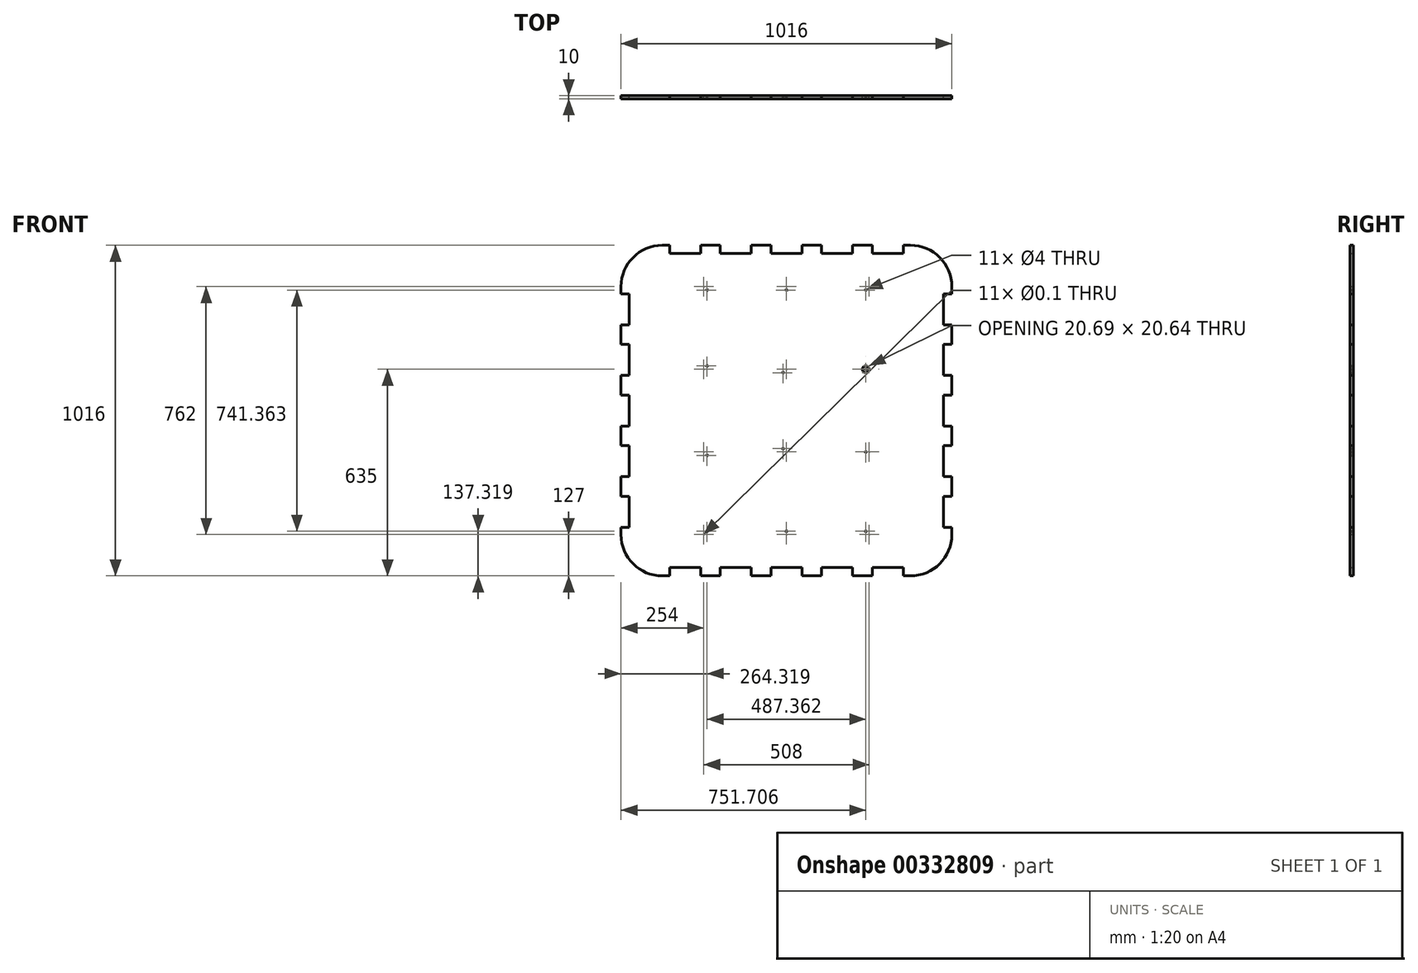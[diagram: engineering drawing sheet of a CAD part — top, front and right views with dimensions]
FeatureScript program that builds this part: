
annotation { "Feature Type Name" : "Feature", "Feature Type Description" : "" }
export const myFeature = defineFeature(function(context is Context, id is Id, definition is map)
    precondition{}
    {
        {
            var Q0;
            Q0=qCreatedBy(makeId("Front.planeOp"),FACE);
            var sketch = newSketch(context, id + "F0", { "sketchPlane" : qUnion([Q0])});
            skLineSegment(sketch, "E0.bottom", {"start": v(508, 508) * mm, "end": v(-508, 508) * mm});
            skLineSegment(sketch, "E0.top", {"start": v(508, -508) * mm, "end": v(-508, -508) * mm});
            skLineSegment(sketch, "E0.left", {"start": v(508, 508) * mm, "end": v(508, -508) * mm});
            skLineSegment(sketch, "E0.right", {"start": v(-508, 508) * mm, "end": v(-508, -508) * mm});
            skPoint(sketch, "E0.middle", {"position": v(0, 0) * mm});
            skCircle(sketch, "E1", {"center": v(-254, 381) * mm, "radius": 0.05 * mm});
            skCircle(sketch, "E2.0.1.0", {"center": v(-254, 127) * mm, "radius": 0.05 * mm});
            skCircle(sketch, "E2.0.2.0", {"center": v(-254, -127) * mm, "radius": 0.05 * mm});
            skCircle(sketch, "E2.1.0.0", {"center": v(0, 381) * mm, "radius": 0.05 * mm});
            skCircle(sketch, "E2.1.1.0", {"center": v(0, 127) * mm, "radius": 0.05 * mm});
            skCircle(sketch, "E2.1.2.0", {"center": v(0, -127) * mm, "radius": 0.05 * mm});
            skCircle(sketch, "E2.2.0.0", {"center": v(254, 381) * mm, "radius": 0.05 * mm});
            skCircle(sketch, "E2.2.1.0", {"center": v(254, 127) * mm, "radius": 0.05 * mm});
            skCircle(sketch, "E2.2.2.0", {"center": v(254, -127) * mm, "radius": 0.05 * mm});
            skLineSegment(sketch, "E2.direction1", {"start": v(-254, 381) * mm, "end": v(0, 381) * mm, "construction": true});
            skLineSegment(sketch, "E2.direction2", {"start": v(-254, 381) * mm, "end": v(-254, 127) * mm, "construction": true});
            skCircle(sketch, "E3.0.0.3", {"center": v(-254, -381) * mm, "radius": 0.05 * mm});
            skCircle(sketch, "E3.0.1.3", {"center": v(0, -381) * mm, "radius": 0.05 * mm});
            skCircle(sketch, "E3.0.2.3", {"center": v(254, -381) * mm, "radius": 0.05 * mm});
            skLineSegment(sketch, "E4", {"start": v(254, 381) * mm, "end": v(0, 381) * mm, "construction": true});
            skLineSegment(sketch, "E5", {"start": v(-254, 381) * mm, "end": v(-254, 126.95) * mm, "construction": true});
            skLineSegment(sketch, "E6", {"start": v(-254, 126.95) * mm, "end": v(0, 127) * mm, "construction": true});
            skLineSegment(sketch, "E7", {"start": v(0, -127) * mm, "end": v(-254, -127) * mm, "construction": true});
            skLineSegment(sketch, "E8", {"start": v(-254, -127) * mm, "end": v(-254, -381) * mm, "construction": true});
            skLineSegment(sketch, "E9", {"start": v(0, 126.95) * mm, "end": v(0, -127) * mm, "construction": true});
            skLineSegment(sketch, "E10", {"start": v(-254, -381) * mm, "end": v(0, -381) * mm, "construction": true});
            skLineSegment(sketch, "E11", {"start": v(0, -381) * mm, "end": v(254, -381) * mm, "construction": true});
            skLineSegment(sketch, "E12", {"start": v(254, -381) * mm, "end": v(254, -127) * mm, "construction": true});
            skLineSegment(sketch, "E13", {"start": v(254, -120.19) * mm, "end": v(254, 127) * mm, "construction": true});
            skLineSegment(sketch, "E14", {"start": v(254, 381) * mm, "end": v(254, 127) * mm, "construction": true});
            skCircle(sketch, "E15", {"center": v(-243.68, 370.68) * mm, "radius": 10.32 * mm});
            skCircle(sketch, "E16", {"center": v(0, 370.68) * mm, "radius": 10.32 * mm});
            skCircle(sketch, "E17", {"center": v(243.68, 370.68) * mm, "radius": 10.32 * mm});
            skCircle(sketch, "E18", {"center": v(-243.68, 370.68) * mm, "radius": 2 * mm});
            skCircle(sketch, "E19", {"center": v(0, 370.68) * mm, "radius": 2 * mm});
            skCircle(sketch, "E20", {"center": v(243.68, 370.68) * mm, "radius": 2 * mm});
            skCircle(sketch, "E21", {"center": v(-243.68, 137.27) * mm, "radius": 10.32 * mm});
            skCircle(sketch, "E22", {"center": v(-243.68, 137.27) * mm, "radius": 2 * mm});
            skCircle(sketch, "E23", {"center": v(-10.32, 116.68) * mm, "radius": 10.32 * mm});
            skCircle(sketch, "E24", {"center": v(-10.32, 116.68) * mm, "radius": 2 * mm});
            skCircle(sketch, "E25.MirrorC", {"center": v(243.68, 127) * mm, "radius": 10.32 * mm});
            skCircle(sketch, "E26.MirrorC", {"center": v(243.68, 127) * mm, "radius": 2 * mm});
            skCircle(sketch, "E27", {"center": v(-10.32, -116.68) * mm, "radius": 10.32 * mm});
            skCircle(sketch, "E28", {"center": v(-10.32, -116.68) * mm, "radius": 2 * mm});
            skCircle(sketch, "E29", {"center": v(-243.68, -137.32) * mm, "radius": 10.32 * mm});
            skCircle(sketch, "E30", {"center": v(-243.68, -137.32) * mm, "radius": 2 * mm});
            skCircle(sketch, "E31", {"center": v(-243.68, -370.68) * mm, "radius": 10.32 * mm});
            skCircle(sketch, "E32", {"center": v(-243.68, -370.68) * mm, "radius": 2 * mm});
            skCircle(sketch, "E33", {"center": v(0, -370.68) * mm, "radius": 2 * mm});
            skCircle(sketch, "E34", {"center": v(0, -370.68) * mm, "radius": 10.32 * mm});
            skCircle(sketch, "E35", {"center": v(243.68, -370.68) * mm, "radius": 10.32 * mm});
            skCircle(sketch, "E36", {"center": v(243.68, -370.68) * mm, "radius": 2 * mm});
            skCircle(sketch, "E37", {"center": v(243.68, -127) * mm, "radius": 2 * mm});
            skCircle(sketch, "E38", {"center": v(243.68, -127) * mm, "radius": 10.32 * mm});
            skLineSegment(sketch, "E39.bottom", {"start": v(-358.77, 508) * mm, "end": v(-263.52, 508) * mm});
            skLineSegment(sketch, "E39.top", {"start": v(-358.77, 482.6) * mm, "end": v(-263.52, 482.6) * mm});
            skLineSegment(sketch, "E39.left", {"start": v(-358.77, 508) * mm, "end": v(-358.77, 482.6) * mm});
            skLineSegment(sketch, "E39.right", {"start": v(-263.52, 508) * mm, "end": v(-263.52, 482.6) * mm});
            skLineSegment(sketch, "E40.bottom", {"start": v(-358.77, -508) * mm, "end": v(-263.52, -508) * mm});
            skLineSegment(sketch, "E40.top", {"start": v(-358.77, -482.6) * mm, "end": v(-263.52, -482.6) * mm});
            skLineSegment(sketch, "E40.left", {"start": v(-358.77, -508) * mm, "end": v(-358.77, -482.6) * mm});
            skLineSegment(sketch, "E40.right", {"start": v(-263.52, -508) * mm, "end": v(-263.52, -482.6) * mm});
            skLineSegment(sketch, "E41.bottom", {"start": v(508, 358.78) * mm, "end": v(482.6, 358.78) * mm});
            skLineSegment(sketch, "E41.top", {"start": v(508, 263.53) * mm, "end": v(482.6, 263.53) * mm});
            skLineSegment(sketch, "E41.left", {"start": v(508, 358.78) * mm, "end": v(508, 263.53) * mm});
            skLineSegment(sketch, "E41.right", {"start": v(482.6, 358.78) * mm, "end": v(482.6, 263.53) * mm});
            skLineSegment(sketch, "E42.bottom", {"start": v(-508, -358.78) * mm, "end": v(-482.6, -358.78) * mm});
            skLineSegment(sketch, "E42.top", {"start": v(-508, -263.53) * mm, "end": v(-482.6, -263.53) * mm});
            skLineSegment(sketch, "E42.left", {"start": v(-508, -358.78) * mm, "end": v(-508, -263.53) * mm});
            skLineSegment(sketch, "E42.right", {"start": v(-482.6, -358.78) * mm, "end": v(-482.6, -263.53) * mm});
            skLineSegment(sketch, "E43.1.0.0", {"start": v(-107.95, 508) * mm, "end": v(-107.95, 482.6) * mm});
            skLineSegment(sketch, "E43.1.0.1", {"start": v(-203.2, 508) * mm, "end": v(-203.2, 482.6) * mm});
            skLineSegment(sketch, "E43.1.0.2", {"start": v(-203.2, 482.6) * mm, "end": v(-107.95, 482.6) * mm});
            skLineSegment(sketch, "E43.2.0.0", {"start": v(47.63, 508) * mm, "end": v(47.63, 482.6) * mm});
            skLineSegment(sketch, "E43.2.0.1", {"start": v(-47.62, 508) * mm, "end": v(-47.62, 482.6) * mm});
            skLineSegment(sketch, "E43.2.0.2", {"start": v(-47.62, 482.6) * mm, "end": v(47.63, 482.6) * mm});
            skLineSegment(sketch, "E43.3.0.0", {"start": v(203.2, 508) * mm, "end": v(203.2, 482.6) * mm});
            skLineSegment(sketch, "E43.3.0.1", {"start": v(107.95, 508) * mm, "end": v(107.95, 482.6) * mm});
            skLineSegment(sketch, "E43.3.0.2", {"start": v(107.95, 482.6) * mm, "end": v(203.2, 482.6) * mm});
            skLineSegment(sketch, "E43.4.0.0", {"start": v(358.78, 508) * mm, "end": v(358.78, 482.6) * mm});
            skLineSegment(sketch, "E43.4.0.1", {"start": v(263.53, 508) * mm, "end": v(263.53, 482.6) * mm});
            skLineSegment(sketch, "E43.4.0.2", {"start": v(263.53, 482.6) * mm, "end": v(358.78, 482.6) * mm});
            skLineSegment(sketch, "E43.direction1", {"start": v(-263.52, 482.6) * mm, "end": v(-107.95, 482.6) * mm, "construction": true});
            skLineSegment(sketch, "E44", {"start": v(-358.77, 495.3) * mm, "end": v(-508, 495.3) * mm, "construction": true});
            skLineSegment(sketch, "E45.0.1.0", {"start": v(508, 203.2) * mm, "end": v(482.6, 203.2) * mm});
            skLineSegment(sketch, "E45.0.1.1", {"start": v(482.6, 203.2) * mm, "end": v(482.6, 107.95) * mm});
            skLineSegment(sketch, "E45.0.1.2", {"start": v(508, 107.95) * mm, "end": v(482.6, 107.95) * mm});
            skLineSegment(sketch, "E45.0.2.0", {"start": v(508, 47.63) * mm, "end": v(482.6, 47.63) * mm});
            skLineSegment(sketch, "E45.0.2.1", {"start": v(482.6, 47.63) * mm, "end": v(482.6, -47.62) * mm});
            skLineSegment(sketch, "E45.0.2.2", {"start": v(508, -47.62) * mm, "end": v(482.6, -47.62) * mm});
            skLineSegment(sketch, "E45.0.3.0", {"start": v(508, -107.95) * mm, "end": v(482.6, -107.95) * mm});
            skLineSegment(sketch, "E45.0.3.1", {"start": v(482.6, -107.95) * mm, "end": v(482.6, -203.2) * mm});
            skLineSegment(sketch, "E45.0.3.2", {"start": v(508, -203.2) * mm, "end": v(482.6, -203.2) * mm});
            skLineSegment(sketch, "E45.0.4.0", {"start": v(508, -263.53) * mm, "end": v(482.6, -263.53) * mm});
            skLineSegment(sketch, "E45.0.4.1", {"start": v(482.6, -263.53) * mm, "end": v(482.6, -358.78) * mm});
            skLineSegment(sketch, "E45.0.4.2", {"start": v(508, -358.78) * mm, "end": v(482.6, -358.78) * mm});
            skLineSegment(sketch, "E45.direction1", {"start": v(482.6, 358.78) * mm, "end": v(494.9, 358.78) * mm, "construction": true});
            skLineSegment(sketch, "E45.direction2", {"start": v(482.6, 358.78) * mm, "end": v(482.6, 203.2) * mm, "construction": true});
            skLineSegment(sketch, "E46.0.1.0", {"start": v(-508, -107.95) * mm, "end": v(-482.6, -107.95) * mm});
            skLineSegment(sketch, "E46.0.1.1", {"start": v(-482.6, -203.2) * mm, "end": v(-482.6, -107.95) * mm});
            skLineSegment(sketch, "E46.0.1.2", {"start": v(-508, -203.2) * mm, "end": v(-482.6, -203.2) * mm});
            skLineSegment(sketch, "E46.0.2.0", {"start": v(-508, 47.62) * mm, "end": v(-482.6, 47.62) * mm});
            skLineSegment(sketch, "E46.0.2.1", {"start": v(-482.6, -47.63) * mm, "end": v(-482.6, 47.62) * mm});
            skLineSegment(sketch, "E46.0.2.2", {"start": v(-508, -47.63) * mm, "end": v(-482.6, -47.63) * mm});
            skLineSegment(sketch, "E46.0.3.0", {"start": v(-508, 203.2) * mm, "end": v(-482.6, 203.2) * mm});
            skLineSegment(sketch, "E46.0.3.1", {"start": v(-482.6, 107.95) * mm, "end": v(-482.6, 203.2) * mm});
            skLineSegment(sketch, "E46.0.3.2", {"start": v(-508, 107.95) * mm, "end": v(-482.6, 107.95) * mm});
            skLineSegment(sketch, "E46.0.4.0", {"start": v(-508, 358.78) * mm, "end": v(-482.6, 358.78) * mm});
            skLineSegment(sketch, "E46.0.4.1", {"start": v(-482.6, 263.53) * mm, "end": v(-482.6, 358.78) * mm});
            skLineSegment(sketch, "E46.0.4.2", {"start": v(-508, 263.53) * mm, "end": v(-482.6, 263.53) * mm});
            skLineSegment(sketch, "E46.direction1", {"start": v(-508, -263.53) * mm, "end": v(-545.7, -263.53) * mm, "construction": true});
            skLineSegment(sketch, "E46.direction2", {"start": v(-508, -263.53) * mm, "end": v(-508, -107.95) * mm, "construction": true});
            skLineSegment(sketch, "E47", {"start": v(494.9, 358.78) * mm, "end": v(494.9, 508) * mm, "construction": true});
            skLineSegment(sketch, "E48", {"start": v(-358.77, -495.3) * mm, "end": v(-508, -495.3) * mm, "construction": true});
            skLineSegment(sketch, "E49.1.0.0", {"start": v(-203.2, -482.6) * mm, "end": v(-107.95, -482.6) * mm});
            skLineSegment(sketch, "E49.1.0.1", {"start": v(-107.95, -508) * mm, "end": v(-107.95, -482.6) * mm});
            skLineSegment(sketch, "E49.1.0.2", {"start": v(-203.2, -508) * mm, "end": v(-203.2, -482.6) * mm});
            skLineSegment(sketch, "E49.2.0.0", {"start": v(-47.62, -482.6) * mm, "end": v(47.63, -482.6) * mm});
            skLineSegment(sketch, "E49.2.0.1", {"start": v(47.63, -508) * mm, "end": v(47.63, -482.6) * mm});
            skLineSegment(sketch, "E49.2.0.2", {"start": v(-47.62, -508) * mm, "end": v(-47.62, -482.6) * mm});
            skLineSegment(sketch, "E49.3.0.0", {"start": v(107.95, -482.6) * mm, "end": v(203.2, -482.6) * mm});
            skLineSegment(sketch, "E49.3.0.1", {"start": v(203.2, -508) * mm, "end": v(203.2, -482.6) * mm});
            skLineSegment(sketch, "E49.3.0.2", {"start": v(107.95, -508) * mm, "end": v(107.95, -482.6) * mm});
            skLineSegment(sketch, "E49.4.0.0", {"start": v(263.53, -482.6) * mm, "end": v(358.78, -482.6) * mm});
            skLineSegment(sketch, "E49.4.0.1", {"start": v(358.78, -508) * mm, "end": v(358.78, -482.6) * mm});
            skLineSegment(sketch, "E49.4.0.2", {"start": v(263.53, -508) * mm, "end": v(263.53, -482.6) * mm});
            skLineSegment(sketch, "E49.direction1", {"start": v(-358.77, -508) * mm, "end": v(-203.2, -508) * mm, "construction": true});
            skLineSegment(sketch, "E50", {"start": v(-495.3, -358.78) * mm, "end": v(-495.3, -508) * mm, "construction": true});
            skSolve(sketch);
        }
        {
            var Q0;
            Q0=makeQuery(id+"F0.imprint","IMPRINT",FACE,{"disambiguationData":[TD([[makeQuery(id+"F0.imprint","IMPRINT",EDGE,{"derivedFrom":sQuery(id+"F0.wireOp",EDGE,"E0.bottom")}),1.0]])]});
            var Q1;
            Q1=makeQuery(id+"F0.imprint","IMPRINT",FACE,{"disambiguationData":[TD([[makeQuery(id+"F0.imprint","IMPRINT",EDGE,{"derivedFrom":sQuery(id+"F0.wireOp",EDGE,"E15")}),1.0]])]});
            var Q2;
            Q2=makeQuery(id+"F0.imprint","IMPRINT",FACE,{"disambiguationData":[TD([[makeQuery(id+"F0.imprint","IMPRINT",EDGE,{"derivedFrom":sQuery(id+"F0.wireOp",EDGE,"E19")}),-1.0]])]});
            var Q3;
            Q3=makeQuery(id+"F0.imprint","IMPRINT",FACE,{"disambiguationData":[TD([[makeQuery(id+"F0.imprint","IMPRINT",EDGE,{"derivedFrom":sQuery(id+"F0.wireOp",EDGE,"E17")}),1.0]])]});
            var Q4;
            Q4=makeQuery(id+"F0.imprint","IMPRINT",FACE,{"disambiguationData":[TD([[makeQuery(id+"F0.imprint","IMPRINT",EDGE,{"derivedFrom":sQuery(id+"F0.wireOp",EDGE,"E21")}),1.0]])]});
            var Q5;
            Q5=makeQuery(id+"F0.imprint","IMPRINT",FACE,{"disambiguationData":[TD([[makeQuery(id+"F0.imprint","IMPRINT",EDGE,{"derivedFrom":sQuery(id+"F0.wireOp",EDGE,"E23")}),1.0]])]});
            var Q6;
            Q6=makeQuery(id+"F0.imprint","IMPRINT",FACE,{"disambiguationData":[TD([[makeQuery(id+"F0.imprint","IMPRINT",EDGE,{"derivedFrom":sQuery(id+"F0.wireOp",EDGE,"E26.MirrorC")}),1.0]])]});
            var Q7;
            Q7=makeQuery(id+"F0.imprint","IMPRINT",FACE,{"disambiguationData":[TD([[makeQuery(id+"F0.imprint","IMPRINT",EDGE,{"derivedFrom":sQuery(id+"F0.wireOp",EDGE,"E29")}),1.0]])]});
            var Q8;
            Q8=makeQuery(id+"F0.imprint","IMPRINT",FACE,{"disambiguationData":[TD([[makeQuery(id+"F0.imprint","IMPRINT",EDGE,{"derivedFrom":sQuery(id+"F0.wireOp",EDGE,"E27")}),1.0]])]});
            var Q9;
            Q9=makeQuery(id+"F0.imprint","IMPRINT",FACE,{"disambiguationData":[TD([[makeQuery(id+"F0.imprint","IMPRINT",EDGE,{"derivedFrom":sQuery(id+"F0.wireOp",EDGE,"E37")}),-1.0]])]});
            var Q10;
            Q10=makeQuery(id+"F0.imprint","IMPRINT",FACE,{"disambiguationData":[TD([[makeQuery(id+"F0.imprint","IMPRINT",EDGE,{"derivedFrom":sQuery(id+"F0.wireOp",EDGE,"E35")}),1.0]])]});
            var Q11;
            Q11=makeQuery(id+"F0.imprint","IMPRINT",FACE,{"disambiguationData":[TD([[makeQuery(id+"F0.imprint","IMPRINT",EDGE,{"derivedFrom":sQuery(id+"F0.wireOp",EDGE,"E33")}),-1.0]])]});
            var Q12;
            Q12=makeQuery(id+"F0.imprint","IMPRINT",FACE,{"disambiguationData":[TD([[makeQuery(id+"F0.imprint","IMPRINT",EDGE,{"derivedFrom":sQuery(id+"F0.wireOp",EDGE,"E31")}),1.0]])]});
            extrude(context, id + "F1", {"entities" : qUnion([Q0, Q1, Q2, Q3, Q4, Q5, Q6, Q7, Q8, Q9, Q10, Q11, Q12]), "depth" : 10 * mm});
        }
        {
            var Q0;
            Q0=makeQuery(id+"F1.opExtrude","SWEPT_EDGE",EDGE,{"disambiguationData":[OSD([sQuery(id+"F0.wireOp",EDGE,"E0.bottom"),sQuery(id+"F0.wireOp",EDGE,"E0.right")])]});
            var Q1;
            Q1=makeQuery(id+"F1.opExtrude","SWEPT_EDGE",EDGE,{"disambiguationData":[OSD([sQuery(id+"F0.wireOp",EDGE,"E0.bottom"),sQuery(id+"F0.wireOp",EDGE,"E0.left")])]});
            var Q2;
            Q2=makeQuery(id+"F1.opExtrude","SWEPT_EDGE",EDGE,{"disambiguationData":[OSD([sQuery(id+"F0.wireOp",EDGE,"E0.top"),sQuery(id+"F0.wireOp",EDGE,"E0.left")])]});
            var Q3;
            Q3=makeQuery(id+"F1.opExtrude","SWEPT_EDGE",EDGE,{"disambiguationData":[OSD([sQuery(id+"F0.wireOp",EDGE,"E0.top"),sQuery(id+"F0.wireOp",EDGE,"E0.right")])]});
            fillet(context, id + "F2", {"entities" : qUnion([Q0, Q1, Q2, Q3]), "radius" : 127 * mm, "tangentPropagation" : true, "allowEdgeOverflow" : false});
        }
    });
